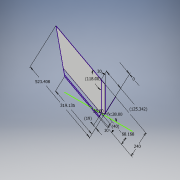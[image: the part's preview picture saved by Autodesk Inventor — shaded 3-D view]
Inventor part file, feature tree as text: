
AUTODESK INVENTOR PART (.ipt)
format: ipt  version: 2019 (Build 230136000, 136)  size: 173,056 bytes
history: native  units: mm
features: sheet_metal_op x3, sketch x2, other x1
ambient origin geometry x8: Origin, YZ Plane, XZ Plane, XY Plane, X Axis, Y Axis, Z Axis, Center Point
bodies: Solid1 (feature_tree)
feature tree (6):
  sketch  "Sketch1"  dims[d0=4.886922mm]
  sheet_metal_op  "Face1"
  sheet_metal_op  "Fold13"
  sheet_metal_op  "Hem1"
  other  "Plate1"
  sketch  "Sketch3"  dims[d6=4.886922mm d7=30.0mm d8=0.5mm d86=0.5mm d87=0.25mm d88=1.0mm d89=0.5mm d90=45.0deg d91=0.5mm d92=20.594885mm d93=0.0mm d94=0.5mm d95=0.25mm d96=1.0mm d97=0.5mm d98=2.0mm d99=0.25mm d100=0.125mm d107=240.0mm d108=18.999754mm d109=40.0mm d110=10.0mm d111=319.134943mm d112=523.407815mm d113=68.168294mm d114=125.34164mm]
